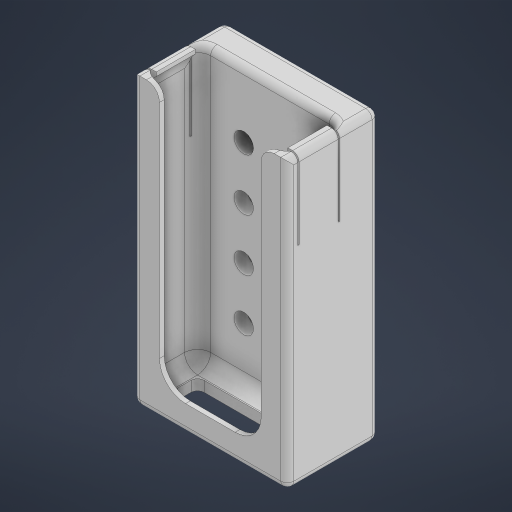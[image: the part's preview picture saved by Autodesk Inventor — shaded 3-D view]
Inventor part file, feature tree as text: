
AUTODESK INVENTOR PART (.ipt)
format: ipt  version: 2023 (Build 270158000, 158)  size: 390,656 bytes
history: native  units: in
note: dims shown in document units (in); Inventor stores cm internally (conversion verified against a paired STEP export)
features: sketch x7, extrude x6, fillet x4, projected_geometry x2, mirror x1, hole x1, pattern_linear x1
ambient origin geometry x8: Origin, YZ Plane, XZ Plane, XY Plane, X Axis, Y Axis, Z Axis, Center Point
bodies: Solid1 (feature_tree)
feature tree (22):
  extrude  "Extrusion1"  Depth=5.3in
  extrude  "Extrusion2"  Depth=1.75in TaperAngle=0.0deg
  extrude  "Extrusion3"  Depth=0.09in
  fillet  "Fillet1"  Radius=0.09in
  extrude  "Extrusion4"  Depth=5.3in TaperAngle=0.0deg
  extrude  "Extrusion5"  Depth=0.5in
  mirror  "Mirror1"
  extrude  "Extrusion6"  Depth=0.5in TaperAngle=0.0deg
  hole  "Hole1"  [1 undecoded]
  pattern_linear  "Rectangular Pattern1"  Spacing1=0.025in  [1 undecoded]
  fillet  "Fillet2"  Radius=0.025in
  fillet  "Fillet3"  Radius=0.75in
  fillet  "Fillet4"  Radius=1.5in
  sketch  "Sketch1"  dims[d0=2.75in d1=5.3in]
  sketch  "Sketch2"  dims[d2=0.1in d3=1.75in d4=0.0in]
  sketch  "Sketch3"  dims[d5=0.09in d6=0.09in d7=0.09in]
  sketch  "Sketch4"  dims[d8=1.05in d9=5.3in d10=0.0in]
  sketch  "Sketch5"  dims[d11=0.5in d12=0.5in]
  projected_geometry  "Projected Loop1"
  sketch  "Sketch6"  dims[d13=0.5in d14=5.25in d15=0.0in]
  projected_geometry  "Projected Loop2"
  sketch  "Sketch7"  dims[d16=0.25in d17=0.2in d18=0.025in d19=0.025in d20=0.75in d21=1.5in d22=0.0in d23=0.0in d30=1.0in d31=0.0in d32=0.125in d33=0.05in d35=0.375in d36=0.375in d37=0.025in d38=0.025in d39=1.0in d40=0.0in d42=0.5in d43=1.5in d44=0.156in d45=0.38in d46=0.375in d47=0.25in d48=0.5635in d49=1.0in d50=0.8108in d51=0.7874in d53=1.0in d54=1.5748in d56=1.0in d57=0.5in d58=0.25in d59=0.125in]
note: 2 required parameter values undecoded (feature->parameter linkage not recoverable at this tier; creation-order binding heuristic only, values carry confidence <= 0.55)
